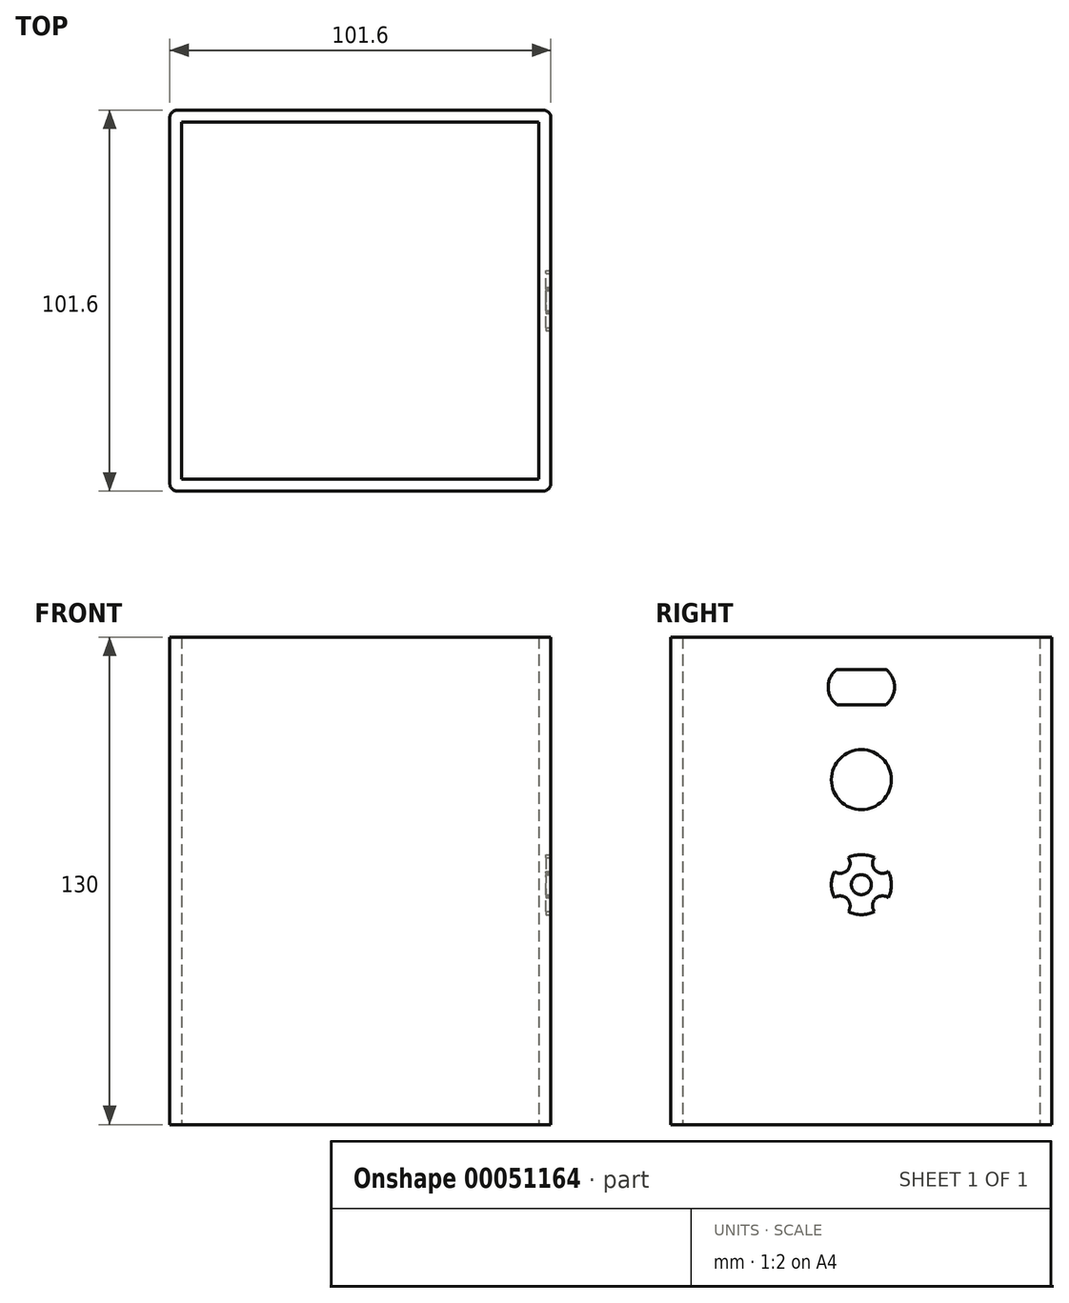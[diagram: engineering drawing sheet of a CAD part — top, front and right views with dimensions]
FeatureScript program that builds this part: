
annotation { "Feature Type Name" : "Feature", "Feature Type Description" : "" }
export const myFeature = defineFeature(function(context is Context, id is Id, definition is map)
    precondition{}
    {
        {
            var Q0;
            Q0=qCreatedBy(makeId("Top.planeOp"),FACE);
            var sketch = newSketch(context, id + "F0", { "sketchPlane" : qUnion([Q0])});
            skLineSegment(sketch, "E0.rect.bottom", {"start": v(50.8, 50.8) * mm, "end": v(-50.8, 50.8) * mm});
            skLineSegment(sketch, "E0.rect.top", {"start": v(50.8, -50.8) * mm, "end": v(-50.8, -50.8) * mm});
            skLineSegment(sketch, "E0.rect.left", {"start": v(50.8, 50.8) * mm, "end": v(50.8, -50.8) * mm});
            skLineSegment(sketch, "E0.rect.right", {"start": v(-50.8, 50.8) * mm, "end": v(-50.8, -50.8) * mm});
            skPoint(sketch, "E0.rect.middle", {"position": v(0, 0) * mm});
            skLineSegment(sketch, "E1.rect.bottom", {"start": v(47.63, 47.63) * mm, "end": v(-47.63, 47.63) * mm});
            skLineSegment(sketch, "E1.rect.top", {"start": v(47.63, -47.62) * mm, "end": v(-47.63, -47.62) * mm});
            skLineSegment(sketch, "E1.rect.left", {"start": v(47.63, 47.63) * mm, "end": v(47.63, -47.62) * mm});
            skLineSegment(sketch, "E1.rect.right", {"start": v(-47.63, 47.63) * mm, "end": v(-47.63, -47.62) * mm});
            skSolve(sketch);
        }
        {
            var Q0;
            Q0=makeQuery(id+"F0.imprint","IMPRINT",FACE,{"disambiguationData":[TD([[makeQuery(id+"F0.imprint","IMPRINT",EDGE,{"derivedFrom":sQuery(id+"F0.wireOp",EDGE,"E0.rect.bottom")}),1.0]])]});
            extrude(context, id + "F1", {"entities" : qUnion([Q0]), "depth" : 130 * mm});
        }
        {
            var Q0;
            Q0=makeQuery(id+"F1.opExtrude","SWEPT_EDGE",EDGE,{"disambiguationData":[OSD([sQuery(id+"F0.wireOp",EDGE,"E0.rect.bottom"),sQuery(id+"F0.wireOp",EDGE,"E0.rect.left")])]});
            var Q1;
            Q1=makeQuery(id+"F1.opExtrude","SWEPT_EDGE",EDGE,{"disambiguationData":[OSD([sQuery(id+"F0.wireOp",EDGE,"E0.rect.bottom"),sQuery(id+"F0.wireOp",EDGE,"E0.rect.right")])]});
            var Q2;
            Q2=makeQuery(id+"F1.opExtrude","SWEPT_EDGE",EDGE,{"disambiguationData":[OSD([sQuery(id+"F0.wireOp",EDGE,"E0.rect.top"),sQuery(id+"F0.wireOp",EDGE,"E0.rect.left")])]});
            var Q3;
            Q3=makeQuery(id+"F1.opExtrude","SWEPT_EDGE",EDGE,{"disambiguationData":[OSD([sQuery(id+"F0.wireOp",EDGE,"E0.rect.top"),sQuery(id+"F0.wireOp",EDGE,"E0.rect.right")])]});
            fillet(context, id + "F2", {"entities" : qUnion([Q0, Q1, Q2, Q3]), "radius" : 2 * mm, "tangentPropagation" : true, "allowEdgeOverflow" : false});
        }
        {
            var Q0;
            Q0=makeQuery(id+"F1.opExtrude","SWEPT_FACE",FACE,{"disambiguationData":[OSD([sQuery(id+"F0.wireOp",EDGE,"E0.rect.left")])]});
            var sketch = newSketch(context, id + "F3", { "sketchPlane" : qUnion([Q0])});
            skLineSegment(sketch, "E2.rect.bottom", {"start": v(6.54, 121.4) * mm, "end": v(-6.54, 121.4) * mm});
            skLineSegment(sketch, "E2.rect.top", {"start": v(6.54, 112) * mm, "end": v(-6.54, 112) * mm});
            skLineSegment(sketch, "E2.rect.left", {"start": v(6.54, 121.4) * mm, "end": v(6.54, 112) * mm});
            skLineSegment(sketch, "E2.rect.right", {"start": v(-6.54, 121.4) * mm, "end": v(-6.54, 112) * mm});
            skPoint(sketch, "E2.rect.middle", {"position": v(0, 116.7) * mm});
            skCircle(sketch, "E3", {"center": v(0, 92) * mm, "radius": 8 * mm});
            skCircle(sketch, "E4", {"center": v(0, 64) * mm, "radius": 8 * mm});
            skLineSegment(sketch, "E5", {"start": v(0, 64) * mm, "end": v(0, 72) * mm});
            skLineSegment(sketch, "E6", {"start": v(0, 72) * mm, "end": v(0, 64) * mm});
            skLineSegment(sketch, "E7", {"start": v(0, 56) * mm, "end": v(0, 64) * mm});
            skLineSegment(sketch, "E8", {"start": v(0, 64) * mm, "end": v(-8, 64) * mm});
            skLineSegment(sketch, "E9", {"start": v(-8, 64) * mm, "end": v(8, 64) * mm});
            skLineSegment(sketch, "E10", {"start": v(8, 64) * mm, "end": v(0, 64) * mm});
            skLineSegment(sketch, "E11", {"start": v(0, 64) * mm, "end": v(5.66, 69.66) * mm});
            skLineSegment(sketch, "E12", {"start": v(5.66, 69.66) * mm, "end": v(0, 64) * mm});
            skLineSegment(sketch, "E13", {"start": v(0, 64) * mm, "end": v(-5.66, 58.34) * mm});
            skPoint(sketch, "E14", {"position": v(8.85, 116.7) * mm});
            skArc(sketch, "E15", {"start": v(6.54, 112) * mm, "mid": v(8.85, 116.7) * mm, "end": v(6.54, 121.4) * mm});
            skPoint(sketch, "E16", {"position": v(-8.85, 116.7) * mm});
            skPoint(sketch, "E16.positionSnap0", {"position": v(-6.54, 116.7) * mm});
            skArc(sketch, "E17", {"start": v(-6.54, 121.4) * mm, "mid": v(-8.85, 116.7) * mm, "end": v(-6.54, 112) * mm});
            skLineSegment(sketch, "E18", {"start": v(0, 130) * mm, "end": v(0, 0) * mm});
            skCircle(sketch, "E19", {"center": v(0, 64) * mm, "radius": 2.67 * mm});
            skLineSegment(sketch, "E20", {"start": v(0, 64) * mm, "end": v(-5.66, 69.66) * mm});
            skLineSegment(sketch, "E21", {"start": v(0, 64) * mm, "end": v(5.66, 58.34) * mm});
            skCircle(sketch, "E22", {"center": v(-5.66, 69.66) * mm, "radius": 2.67 * mm});
            skCircle(sketch, "E23", {"center": v(5.66, 69.66) * mm, "radius": 2.67 * mm});
            skCircle(sketch, "E24", {"center": v(5.66, 58.34) * mm, "radius": 2.67 * mm});
            skCircle(sketch, "E25", {"center": v(-5.66, 58.34) * mm, "radius": 2.67 * mm});
            skCircle(sketch, "E26", {"center": v(0, 92) * mm, "radius": 9 * mm});
            skSolve(sketch);
        }
        {
            var Q0;
            {var subQ1=sQuery(id+"F3.wireOp",EDGE,"E2.rect.right");Q0=makeQuery(id+"F3.imprint","IMPRINT",FACE,{"disambiguationData":[TD([[makeQuery(id+"F3.imprint","IMPRINT",EDGE,{"derivedFrom":subQ1}),1.0]])]});}
            var Q1;
            Q1=makeQuery(id+"F3.imprint","IMPRINT",FACE,{"disambiguationData":[TD([[makeQuery(id+"F3.imprint","IMPRINT",EDGE,{"derivedFrom":sQuery(id+"F3.wireOp",EDGE,"E2.rect.right")}),-1.0]])]});
            var Q2;
            {var subQ1=sQuery(id+"F3.wireOp",EDGE,"E2.rect.left");Q2=makeQuery(id+"F3.imprint","IMPRINT",FACE,{"disambiguationData":[TD([[makeQuery(id+"F3.imprint","IMPRINT",EDGE,{"derivedFrom":subQ1}),-1.0]])]});}
            var Q3;
            Q3=makeQuery(id+"F3.imprint","IMPRINT",FACE,{"disambiguationData":[TD([[makeQuery(id+"F3.imprint","IMPRINT",EDGE,{"derivedFrom":sQuery(id+"F3.wireOp",EDGE,"E2.rect.left")}),1.0]])]});
            var Q4;
            {var subQ0=sQuery(id+"F3.wireOp",EDGE,"E18");var subQ1=sQuery(id+"F3.wireOp",EDGE,"E3");var subQ2=makeQuery(id+"F3.imprint","INTERSECT",VERTEX,{"disambiguationData":[OD(0.0)],"derivedFrom":[subQ1,subQ0]});Q4=makeQuery(id+"F3.imprint","IMPRINT",FACE,{"disambiguationData":[TD([[makeQuery(id+"F3.imprint","IMPRINT",EDGE,{"disambiguationData":[TD([[subQ2,-1.0]])],"derivedFrom":subQ1}),1.0]])]});}
            var Q5;
            {var subQ0=sQuery(id+"F3.wireOp",EDGE,"E18");var subQ1=sQuery(id+"F3.wireOp",EDGE,"E3");var subQ2=makeQuery(id+"F3.imprint","INTERSECT",VERTEX,{"disambiguationData":[OD(0.0)],"derivedFrom":[subQ1,subQ0]});Q5=makeQuery(id+"F3.imprint","IMPRINT",FACE,{"disambiguationData":[TD([[makeQuery(id+"F3.imprint","IMPRINT",EDGE,{"disambiguationData":[TD([[subQ2,1.0]])],"derivedFrom":subQ1}),1.0]])]});}
            extrude(context, id + "F4", {"entities" : qUnion([Q0, Q1, Q2, Q3, Q4, Q5]), "operationType" : NewBodyOperationType.REMOVE, "oppositeDirection" : true, "depth" : 1 / 203.2 * mm});
        }
        {
            var Q0;
            Q0=makeQuery(id+"F1.opExtrude","SWEPT_FACE",FACE,{"disambiguationData":[OSD([sQuery(id+"F0.wireOp",EDGE,"E0.rect.left")])]});
            var sketch = newSketch(context, id + "F5", { "sketchPlane" : qUnion([Q0])});
            skArc(sketch, "E27", {"start": v(-7.2, 67.48) * mm, "mid": v(-8, 64) * mm, "end": v(-7.2, 60.52) * mm});
            skLineSegment(sketch, "E28", {"start": v(0, 136.53) * mm, "end": v(0, 84) * mm});
            skCircle(sketch, "E29", {"center": v(0, 64) * mm, "radius": 2.67 * mm});
            skArc(sketch, "E30", {"start": v(-7.2, 67.48) * mm, "mid": v(-3.77, 67.77) * mm, "end": v(-3.48, 71.2) * mm});
            skArc(sketch, "E31", {"start": v(3.48, 71.2) * mm, "mid": v(3.77, 67.77) * mm, "end": v(7.2, 67.48) * mm});
            skArc(sketch, "E32", {"start": v(7.2, 60.52) * mm, "mid": v(3.77, 60.23) * mm, "end": v(3.48, 56.8) * mm});
            skArc(sketch, "E33", {"start": v(-3.48, 56.8) * mm, "mid": v(-3.77, 60.23) * mm, "end": v(-7.2, 60.52) * mm});
            skLineSegment(sketch, "E34.0", {"start": v(50.8, 130) * mm, "end": v(50.8, 0) * mm});
            skLineSegment(sketch, "E35.0", {"start": v(-50.8, 0) * mm, "end": v(-50.8, 130) * mm});
            skCircle(sketch, "E36.0", {"center": v(0, 92) * mm, "radius": 8 * mm});
            skArc(sketch, "E37.trimOffspring", {"start": v(3.48, 71.2) * mm, "mid": v(0, 72) * mm, "end": v(-3.48, 71.2) * mm});
            skArc(sketch, "E38.trimOffspring", {"start": v(7.2, 60.52) * mm, "mid": v(8, 64) * mm, "end": v(7.2, 67.48) * mm});
            skArc(sketch, "E39.trimOffspring", {"start": v(-3.48, 56.8) * mm, "mid": v(0, 56) * mm, "end": v(3.48, 56.8) * mm});
            skSolve(sketch);
        }
        {
            var Q0;
            {var subQ0=sQuery(id+"F5.wireOp",EDGE,"E36.0");var subQ1=sQuery(id+"F5.wireOp",EDGE,"E28");var subQ2=makeQuery(id+"F5.imprint","INTERSECT",VERTEX,{"disambiguationData":[OD(0.0)],"derivedFrom":[subQ1,subQ0]});Q0=makeQuery(id+"F5.imprint","IMPRINT",FACE,{"disambiguationData":[TD([[makeQuery(id+"F5.imprint","IMPRINT",EDGE,{"disambiguationData":[TD([[subQ2,1.0]])],"derivedFrom":subQ1}),-1.0]])]});}
            var Q1;
            {var subQ0=sQuery(id+"F5.wireOp",EDGE,"E36.0");var subQ1=sQuery(id+"F5.wireOp",EDGE,"E28");var subQ2=makeQuery(id+"F5.imprint","INTERSECT",VERTEX,{"disambiguationData":[OD(0.0)],"derivedFrom":[subQ1,subQ0]});Q1=makeQuery(id+"F5.imprint","IMPRINT",FACE,{"disambiguationData":[TD([[makeQuery(id+"F5.imprint","IMPRINT",EDGE,{"disambiguationData":[TD([[subQ2,1.0]])],"derivedFrom":subQ1}),1.0]])]});}
            var Q2;
            Q2=makeQuery(id+"F5.imprint","IMPRINT",FACE,{"disambiguationData":[TD([[makeQuery(id+"F5.imprint","IMPRINT",EDGE,{"derivedFrom":sQuery(id+"F5.wireOp",EDGE,"E27")}),1.0]])]});
            extrude(context, id + "F6", {"entities" : qUnion([Q0, Q1, Q2]), "operationType" : NewBodyOperationType.REMOVE, "oppositeDirection" : true, "depth" : 1.27 * mm});
        }
    });
